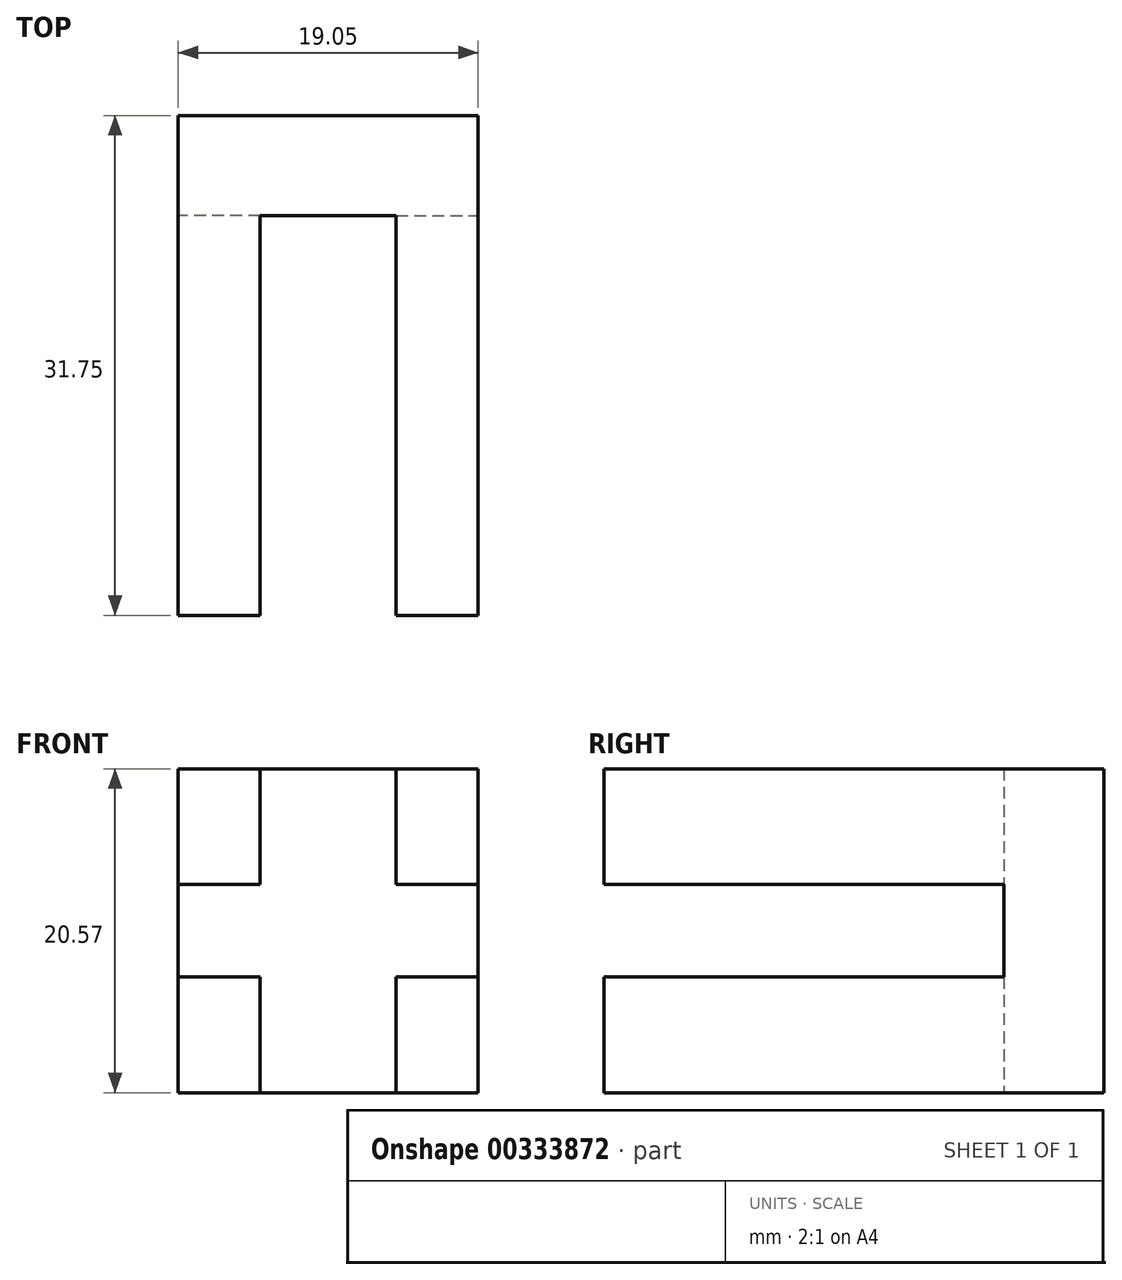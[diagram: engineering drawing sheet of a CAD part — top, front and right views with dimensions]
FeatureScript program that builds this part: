
annotation { "Feature Type Name" : "Feature", "Feature Type Description" : "" }
export const myFeature = defineFeature(function(context is Context, id is Id, definition is map)
    precondition{}
    {
        {
            var Q0;
            Q0=qCreatedBy(makeId("Front.planeOp"),FACE);
            var sketch = newSketch(context, id + "F0", { "sketchPlane" : qUnion([Q0])});
            skLineSegment(sketch, "E0.bottom", {"start": v(0, 0) * mm, "end": v(19.05, 0) * mm});
            skLineSegment(sketch, "E0.top", {"start": v(0, 20.57) * mm, "end": v(19.05, 20.57) * mm});
            skLineSegment(sketch, "E0.left", {"start": v(0, 0) * mm, "end": v(0, 20.57) * mm});
            skLineSegment(sketch, "E0.right", {"start": v(19.05, 0) * mm, "end": v(19.05, 20.57) * mm});
            skSolve(sketch);
        }
        {
            var Q0;
            Q0 = qSketchRegion(id + "F0", true);
            extrude(context, id + "F1", {"entities" : qUnion([Q0]), "depth" : 6.35 * mm});
        }
        {
            var Q0;
            Q0=makeQuery(id+"F1.opExtrude","CAP_FACE",FACE,{"disambiguationData":[OSD([sQuery(id+"F0.wireOp",EDGE,"E0.bottom"),sQuery(id+"F0.wireOp",EDGE,"E0.top"),sQuery(id+"F0.wireOp",EDGE,"E0.left"),sQuery(id+"F0.wireOp",EDGE,"E0.right")])],"isStart":false});
            var sketch = newSketch(context, id + "F2", { "sketchPlane" : qUnion([Q0])});
            skLineSegment(sketch, "E1.0", {"start": v(0, 20.57) * mm, "end": v(5.2, 20.57) * mm});
            skLineSegment(sketch, "E2.0", {"start": v(19.05, 0) * mm, "end": v(19.05, 7.35) * mm});
            skLineSegment(sketch, "E3.0", {"start": v(0, 0) * mm, "end": v(5.2, 0) * mm});
            skLineSegment(sketch, "E4.0", {"start": v(0, 0) * mm, "end": v(0, 7.35) * mm});
            skLineSegment(sketch, "E5", {"start": v(13.84, 20.57) * mm, "end": v(13.84, 13.23) * mm});
            skLineSegment(sketch, "E6", {"start": v(13.84, 13.23) * mm, "end": v(19.05, 13.23) * mm});
            skPoint(sketch, "E7.end.orphan", {"position": v(9.52, 20.57) * mm});
            skLineSegment(sketch, "E8", {"start": v(5.2, 20.57) * mm, "end": v(5.2, 13.23) * mm});
            skLineSegment(sketch, "E9", {"start": v(5.2, 13.23) * mm, "end": v(0, 13.23) * mm});
            skLineSegment(sketch, "E10", {"start": v(0, 13.23) * mm, "end": v(0, 7.35) * mm});
            skLineSegment(sketch, "E11", {"start": v(0, 7.35) * mm, "end": v(5.2, 7.35) * mm});
            skLineSegment(sketch, "E12", {"start": v(5.2, 7.35) * mm, "end": v(5.2, 0) * mm});
            skLineSegment(sketch, "E13", {"start": v(13.84, 7.35) * mm, "end": v(19.05, 7.35) * mm});
            skPoint(sketch, "E14.end.orphan", {"position": v(9.53, 3.67) * mm});
            skPoint(sketch, "E15.orphan", {"position": v(9.53, 0) * mm});
            skLineSegment(sketch, "E16.trimOffspring", {"start": v(19.05, 13.23) * mm, "end": v(19.05, 20.57) * mm});
            skLineSegment(sketch, "E17.trimOffspring", {"start": v(13.84, 0) * mm, "end": v(19.05, 0) * mm});
            skLineSegment(sketch, "E18.trimOffspring", {"start": v(0, 13.23) * mm, "end": v(0, 20.57) * mm});
            skLineSegment(sketch, "E19.trimOffspring", {"start": v(13.84, 20.57) * mm, "end": v(19.05, 20.57) * mm});
            skLineSegment(sketch, "E20", {"start": v(13.84, 0) * mm, "end": v(13.84, 7.35) * mm});
            skPoint(sketch, "E21.orphan", {"position": v(9.52, 7.35) * mm});
            skSolve(sketch);
        }
        {
            var Q0;
            Q0 = qSketchRegion(id + "F2", true);
            extrude(context, id + "F3", {"entities" : qUnion([Q0]), "operationType" : NewBodyOperationType.ADD, "depth" : 25.4 * mm});
        }
    });
